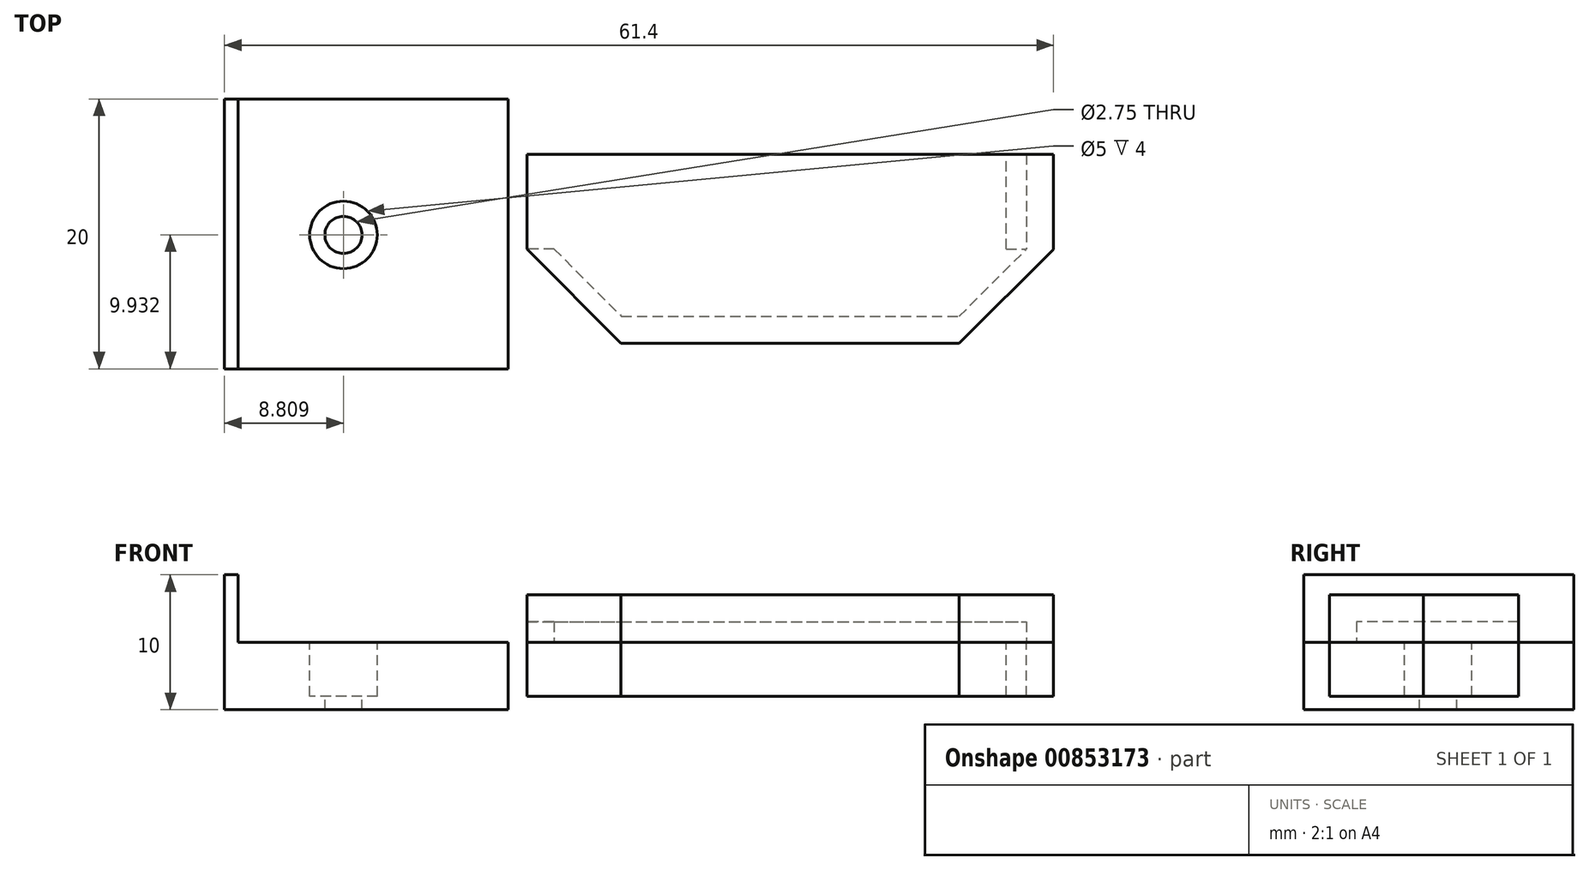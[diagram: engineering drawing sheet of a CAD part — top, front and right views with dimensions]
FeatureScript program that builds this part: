
annotation { "Feature Type Name" : "Feature", "Feature Type Description" : "" }
export const myFeature = defineFeature(function(context is Context, id is Id, definition is map)
    precondition{}
    {
        {
            var Q0;
            Q0=qCreatedBy(makeId("Top.planeOp"),FACE);
            var sketch = newSketch(context, id + "F0", { "sketchPlane" : qUnion([Q0])});
            skLineSegment(sketch, "E0.bottom", {"start": v(-4.97, -1.67) * mm, "end": v(30.03, -1.67) * mm});
            skLineSegment(sketch, "E0.top", {"start": v(-4.97, -8.67) * mm, "end": v(30.03, -8.67) * mm});
            skLineSegment(sketch, "E0.left", {"start": v(-4.97, -1.67) * mm, "end": v(-4.97, -8.67) * mm});
            skLineSegment(sketch, "E0.right", {"start": v(30.03, -1.67) * mm, "end": v(30.03, -8.67) * mm});
            skLineSegment(sketch, "E1", {"start": v(-4.97, -8.67) * mm, "end": v(0.03, -13.67) * mm});
            skLineSegment(sketch, "E2", {"start": v(0.03, -13.67) * mm, "end": v(25.03, -13.67) * mm});
            skLineSegment(sketch, "E3", {"start": v(25.03, -13.67) * mm, "end": v(30.03, -8.67) * mm});
            skLineSegment(sketch, "E4", {"start": v(0.03, -13.67) * mm, "end": v(0.03, -8.67) * mm});
            skLineSegment(sketch, "E5", {"start": v(25.03, -13.67) * mm, "end": v(25.03, -8.67) * mm});
            skLineSegment(sketch, "E6", {"start": v(-4.97, -1.67) * mm, "end": v(-6.97, -1.67) * mm});
            skLineSegment(sketch, "E7", {"start": v(-6.97, -1.67) * mm, "end": v(-6.97, -8.67) * mm});
            skLineSegment(sketch, "E8", {"start": v(-6.97, -8.67) * mm, "end": v(0, -15.67) * mm});
            skLineSegment(sketch, "E9", {"start": v(0, -15.67) * mm, "end": v(25.05, -15.67) * mm});
            skLineSegment(sketch, "E10", {"start": v(25.05, -15.67) * mm, "end": v(32.03, -8.71) * mm});
            skLineSegment(sketch, "E11", {"start": v(32.03, -8.71) * mm, "end": v(32.03, -1.67) * mm});
            skLineSegment(sketch, "E12", {"start": v(32.03, -1.67) * mm, "end": v(30.03, -1.67) * mm});
            skLineSegment(sketch, "E13", {"start": v(0, -15.67) * mm, "end": v(0.03, -13.67) * mm});
            skLineSegment(sketch, "E14", {"start": v(-4.97, -8.67) * mm, "end": v(-6.97, -8.67) * mm});
            skLineSegment(sketch, "E15", {"start": v(25.05, -15.67) * mm, "end": v(25.03, -13.67) * mm});
            skLineSegment(sketch, "E16", {"start": v(30.03, -8.67) * mm, "end": v(32.03, -8.71) * mm});
            skLineSegment(sketch, "E17", {"start": v(28.53, -8.67) * mm, "end": v(28.53, -1.67) * mm});
            skSolve(sketch);
        }
        {
            var Q0;
            Q0=makeQuery(id+"F0.imprint","IMPRINT",FACE,{"disambiguationData":[TD([[makeQuery(id+"F0.imprint","IMPRINT",EDGE,{"derivedFrom":sQuery(id+"F0.wireOp",EDGE,"E0.left")}),-1.0]])]});
            var Q1;
            Q1=makeQuery(id+"F0.imprint","IMPRINT",FACE,{"disambiguationData":[TD([[makeQuery(id+"F0.imprint","IMPRINT",EDGE,{"derivedFrom":sQuery(id+"F0.wireOp",EDGE,"E0.right")}),1.0]])]});
            var Q2;
            Q2=makeQuery(id+"F0.imprint","IMPRINT",FACE,{"disambiguationData":[TD([[makeQuery(id+"F0.imprint","IMPRINT",EDGE,{"derivedFrom":sQuery(id+"F0.wireOp",EDGE,"E1")}),-1.0]])]});
            var Q3;
            Q3=makeQuery(id+"F0.imprint","IMPRINT",FACE,{"disambiguationData":[TD([[makeQuery(id+"F0.imprint","IMPRINT",EDGE,{"derivedFrom":sQuery(id+"F0.wireOp",EDGE,"E2")}),-1.0]])]});
            var Q4;
            Q4=makeQuery(id+"F0.imprint","IMPRINT",FACE,{"disambiguationData":[TD([[makeQuery(id+"F0.imprint","IMPRINT",EDGE,{"derivedFrom":sQuery(id+"F0.wireOp",EDGE,"E3")}),-1.0]])]});
            var Q5;
            Q5=makeQuery(id+"F0.imprint","IMPRINT",FACE,{"disambiguationData":[TD([[makeQuery(id+"F0.imprint","IMPRINT",EDGE,{"derivedFrom":sQuery(id+"F0.wireOp",EDGE,"E2")}),1.0]])]});
            var Q6;
            {var subQ0=sQuery(id+"F0.wireOp",EDGE,"E1");Q6=makeQuery(id+"F0.imprint","IMPRINT",FACE,{"disambiguationData":[TD([[makeQuery(id+"F0.imprint","IMPRINT",EDGE,{"derivedFrom":subQ0}),1.0]])]});}
            var Q7;
            {var subQ0=sQuery(id+"F0.wireOp",EDGE,"E3");Q7=makeQuery(id+"F0.imprint","IMPRINT",FACE,{"disambiguationData":[TD([[makeQuery(id+"F0.imprint","IMPRINT",EDGE,{"derivedFrom":subQ0}),1.0]])]});}
            var Q8;
            Q8=makeQuery(id+"F0.imprint","IMPRINT",FACE,{"disambiguationData":[TD([[makeQuery(id+"F0.imprint","IMPRINT",EDGE,{"derivedFrom":sQuery(id+"F0.wireOp",EDGE,"E0.bottom")}),-1.0]])]});
            var Q9;
            {var subQ4=sQuery(id+"F0.wireOp",EDGE,"E0.left");Q9=makeQuery(id+"F0.imprint","IMPRINT",FACE,{"disambiguationData":[TD([[makeQuery(id+"F0.imprint","IMPRINT",EDGE,{"derivedFrom":subQ4}),1.0]])]});}
            extrude(context, id + "F1", {"entities" : qUnion([Q0, Q1, Q2, Q3, Q4, Q5, Q6, Q7, Q8, Q9]), "depth" : 3.5 * mm, "offsetDistance" : 25 * mm});
        }
        {
            var Q0;
            {var subQ0=sQuery(id+"F0.wireOp",EDGE,"E0.right");Q0=makeQuery(id+"F0.imprint","IMPRINT",FACE,{"disambiguationData":[TD([[makeQuery(id+"F0.imprint","IMPRINT",EDGE,{"derivedFrom":subQ0}),-1.0]])]});}
            var Q1;
            {var subQ4=sQuery(id+"F0.wireOp",EDGE,"E0.left");Q1=makeQuery(id+"F0.imprint","IMPRINT",FACE,{"disambiguationData":[TD([[makeQuery(id+"F0.imprint","IMPRINT",EDGE,{"derivedFrom":subQ4}),1.0]])]});}
            var Q2;
            {var subQ3=sQuery(id+"F0.wireOp",EDGE,"E3");Q2=makeQuery(id+"F0.imprint","IMPRINT",FACE,{"disambiguationData":[TD([[makeQuery(id+"F0.imprint","IMPRINT",EDGE,{"derivedFrom":subQ3}),1.0]])]});}
            var Q3;
            Q3=makeQuery(id+"F0.imprint","IMPRINT",FACE,{"disambiguationData":[TD([[makeQuery(id+"F0.imprint","IMPRINT",EDGE,{"derivedFrom":sQuery(id+"F0.wireOp",EDGE,"E2")}),1.0]])]});
            var Q4;
            {var subQ0=sQuery(id+"F0.wireOp",EDGE,"E1");Q4=makeQuery(id+"F0.imprint","IMPRINT",FACE,{"disambiguationData":[TD([[makeQuery(id+"F0.imprint","IMPRINT",EDGE,{"derivedFrom":subQ0}),1.0]])]});}
            var Q5;
            Q5=makeQuery(id+"F0.imprint","IMPRINT",FACE,{"disambiguationData":[TD([[makeQuery(id+"F0.imprint","IMPRINT",EDGE,{"derivedFrom":sQuery(id+"F0.wireOp",EDGE,"E0.left")}),-1.0]])]});
            extrude(context, id + "F2", {"entities" : qUnion([Q0, Q1, Q2, Q3, Q4, Q5]), "operationType" : NewBodyOperationType.REMOVE, "depth" : 1.5 * mm, "offsetDistance" : 25 * mm});
        }
        {
            var Q0;
            Q0=makeQuery(id+"F0.imprint","IMPRINT",FACE,{"disambiguationData":[TD([[makeQuery(id+"F0.imprint","IMPRINT",EDGE,{"derivedFrom":sQuery(id+"F0.wireOp",EDGE,"E0.right")}),1.0]])]});
            var Q1;
            Q1=makeQuery(id+"F0.imprint","IMPRINT",FACE,{"disambiguationData":[TD([[makeQuery(id+"F0.imprint","IMPRINT",EDGE,{"derivedFrom":sQuery(id+"F0.wireOp",EDGE,"E3")}),-1.0]])]});
            var Q2;
            {var subQ3=sQuery(id+"F0.wireOp",EDGE,"E3");Q2=makeQuery(id+"F0.imprint","IMPRINT",FACE,{"disambiguationData":[TD([[makeQuery(id+"F0.imprint","IMPRINT",EDGE,{"derivedFrom":subQ3}),1.0]])]});}
            var Q3;
            {var subQ4=sQuery(id+"F0.wireOp",EDGE,"E0.left");Q3=makeQuery(id+"F0.imprint","IMPRINT",FACE,{"disambiguationData":[TD([[makeQuery(id+"F0.imprint","IMPRINT",EDGE,{"derivedFrom":subQ4}),1.0]])]});}
            var Q4;
            Q4=makeQuery(id+"F0.imprint","IMPRINT",FACE,{"disambiguationData":[TD([[makeQuery(id+"F0.imprint","IMPRINT",EDGE,{"derivedFrom":sQuery(id+"F0.wireOp",EDGE,"E2")}),1.0]])]});
            var Q5;
            Q5=makeQuery(id+"F0.imprint","IMPRINT",FACE,{"disambiguationData":[TD([[makeQuery(id+"F0.imprint","IMPRINT",EDGE,{"derivedFrom":sQuery(id+"F0.wireOp",EDGE,"E2")}),-1.0]])]});
            var Q6;
            Q6=makeQuery(id+"F0.imprint","IMPRINT",FACE,{"disambiguationData":[TD([[makeQuery(id+"F0.imprint","IMPRINT",EDGE,{"derivedFrom":sQuery(id+"F0.wireOp",EDGE,"E1")}),-1.0]])]});
            var Q7;
            {var subQ0=sQuery(id+"F0.wireOp",EDGE,"E1");Q7=makeQuery(id+"F0.imprint","IMPRINT",FACE,{"disambiguationData":[TD([[makeQuery(id+"F0.imprint","IMPRINT",EDGE,{"derivedFrom":subQ0}),1.0]])]});}
            var Q8;
            Q8=makeQuery(id+"F0.imprint","IMPRINT",FACE,{"disambiguationData":[TD([[makeQuery(id+"F0.imprint","IMPRINT",EDGE,{"derivedFrom":sQuery(id+"F0.wireOp",EDGE,"E0.left")}),-1.0]])]});
            extrude(context, id + "F3", {"entities" : qUnion([Q0, Q1, Q2, Q3, Q4, Q5, Q6, Q7, Q8]), "oppositeDirection" : true, "depth" : 4 * mm, "offsetDistance" : 25 * mm});
        }
        {
            var Q0;
            Q0=qCreatedBy(makeId("Top.planeOp"),FACE);
            var sketch = newSketch(context, id + "F4", { "sketchPlane" : qUnion([Q0])});
            skLineSegment(sketch, "E18.bottom", {"start": v(-28.37, 2.44) * mm, "end": v(-8.37, 2.44) * mm});
            skLineSegment(sketch, "E18.top", {"start": v(-28.37, -17.56) * mm, "end": v(-8.37, -17.56) * mm});
            skLineSegment(sketch, "E18.left", {"start": v(-28.37, 2.44) * mm, "end": v(-28.37, -17.56) * mm});
            skLineSegment(sketch, "E18.right", {"start": v(-8.37, 2.44) * mm, "end": v(-8.37, -17.56) * mm});
            skLineSegment(sketch, "E19", {"start": v(-28.37, 2.44) * mm, "end": v(-29.37, 2.44) * mm});
            skLineSegment(sketch, "E20", {"start": v(-28.37, -17.56) * mm, "end": v(-29.37, -17.56) * mm});
            skLineSegment(sketch, "E21", {"start": v(-29.37, -17.56) * mm, "end": v(-29.37, 2.44) * mm});
            skSolve(sketch);
        }
        {
            var Q0;
            Q0=makeQuery(id+"F4.imprint","IMPRINT",FACE,{"disambiguationData":[TD([[makeQuery(id+"F4.imprint","IMPRINT",EDGE,{"derivedFrom":sQuery(id+"F4.wireOp",EDGE,"E18.left")}),-1.0]])]});
            extrude(context, id + "F5", {"entities" : qUnion([Q0]), "depth" : 5 * mm, "offsetDistance" : 25 * mm});
        }
        {
            var Q0;
            Q0=makeQuery(id+"F4.imprint","IMPRINT",FACE,{"disambiguationData":[TD([[makeQuery(id+"F4.imprint","IMPRINT",EDGE,{"derivedFrom":sQuery(id+"F4.wireOp",EDGE,"E18.bottom")}),-1.0]])]});
            var Q1;
            Q1=makeQuery(id+"F4.imprint","IMPRINT",FACE,{"disambiguationData":[TD([[makeQuery(id+"F4.imprint","IMPRINT",EDGE,{"derivedFrom":sQuery(id+"F4.wireOp",EDGE,"E18.left")}),-1.0]])]});
            extrude(context, id + "F6", {"entities" : qUnion([Q0, Q1]), "operationType" : NewBodyOperationType.ADD, "oppositeDirection" : true, "depth" : 5 * mm, "offsetDistance" : 25 * mm});
        }
        {
            var Q0;
            Q0=qCreatedBy(makeId("Top.planeOp"),FACE);
            var sketch = newSketch(context, id + "F7", { "sketchPlane" : qUnion([Q0])});
            skCircle(sketch, "E22", {"center": v(-20.56, -7.63) * mm, "radius": 1.25 * mm});
            skCircle(sketch, "E23", {"center": v(-20.56, -7.63) * mm, "radius": 2.8 * mm});
            skSolve(sketch);
        }
        {
            var Q0;
            Q0=sQuery(id+"F7.wireOp",VERTEX,"E22.center");
            var Q1;
            Q1=sQuery(id+"F7.wireOp",VERTEX,"E22.center");
            var Q2;
            Q2=makeQuery(id+"F5.opExtrude","SWEPT_BODY",BODY,{"disambiguationData":[OSD([sQuery(id+"F4.wireOp",EDGE,"E18.left"),sQuery(id+"F4.wireOp",EDGE,"E19"),sQuery(id+"F4.wireOp",EDGE,"E20"),sQuery(id+"F4.wireOp",EDGE,"E21")])]});
            hole(context, id + "F8", {"style" : HoleStyle.C_BORE, "endStyle" : HoleEndStyle.THROUGH, "holeDiameter" : 2.75 * mm, "cBoreDiameter" : 5 * mm, "cBoreDepth" : 4 * mm, "majorDiameter" : 5 * mm, "isTappedThrough" : true, "tappedDepth" : 12 * mm, "tapClearance" : 3, "locations" : qUnion([Q0, Q1]), "scope" : qUnion([Q2])});
        }
    });
